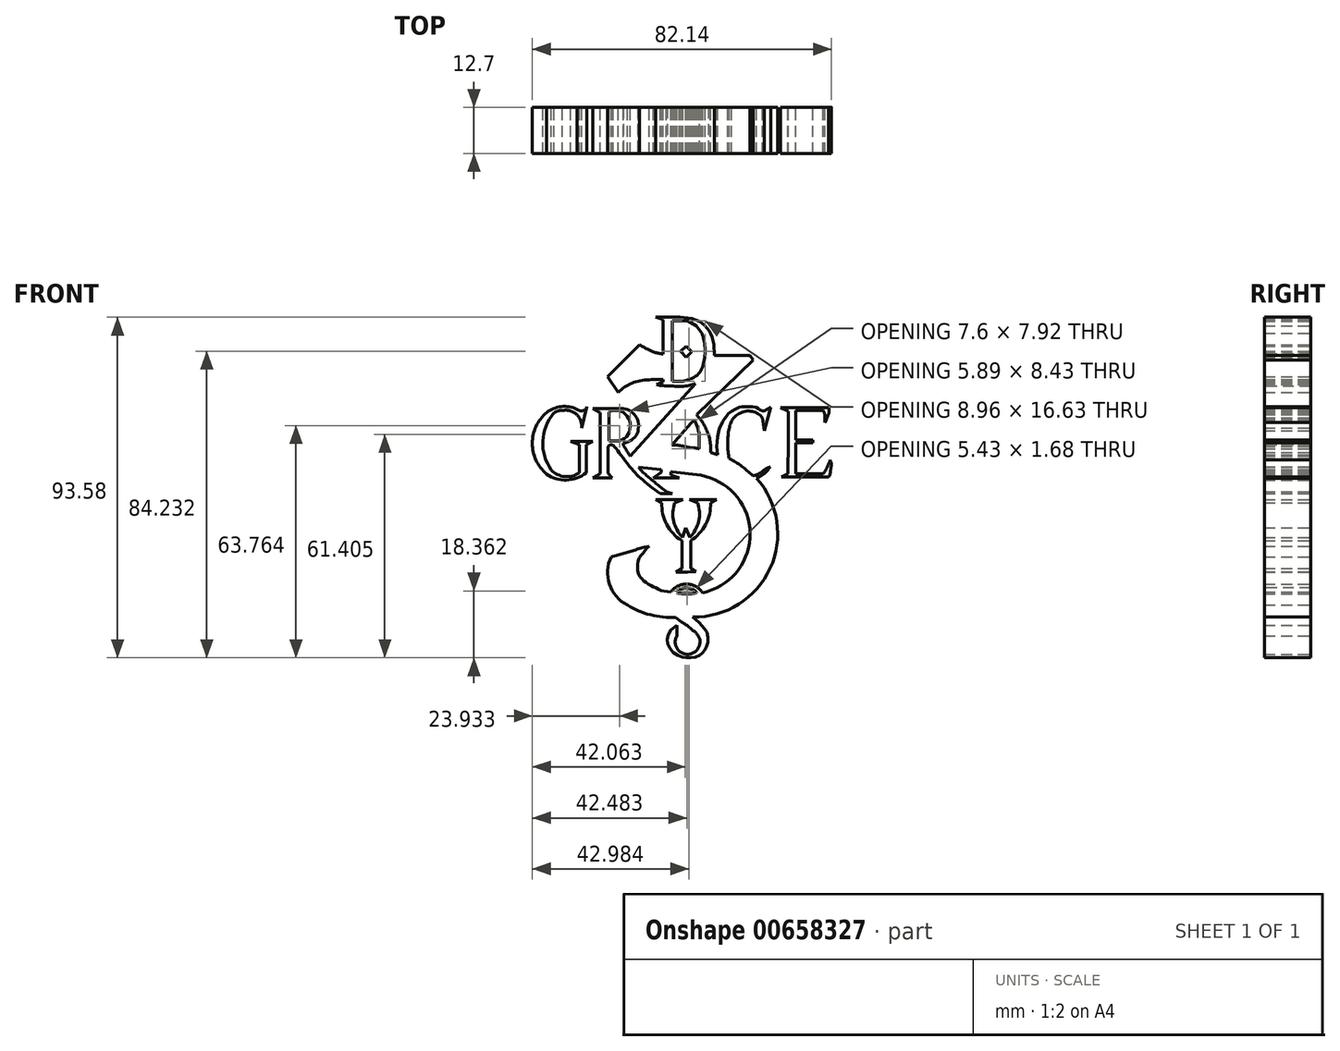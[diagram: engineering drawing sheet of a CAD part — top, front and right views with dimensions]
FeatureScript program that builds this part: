
annotation { "Feature Type Name" : "Feature", "Feature Type Description" : "" }
export const myFeature = defineFeature(function(context is Context, id is Id, definition is map)
    precondition{}
    {
        {
            var Q0;
            Q0=qCreatedBy(makeId("Front.planeOp"),FACE);
            var sketch = newSketch(context, id + "F0", { "sketchPlane" : qUnion([Q0])});
            skLineSegment(sketch, "E0", {"start": v(-8.84, 46.14) * mm, "end": v(-6.93, 45.57) * mm});
            skLineSegment(sketch, "E1", {"start": v(-6.93, 45.57) * mm, "end": v(-6.8, 45.06) * mm});
            skLineSegment(sketch, "E2", {"start": v(-6.8, 45.06) * mm, "end": v(-6.8, 28.36) * mm});
            skLineSegment(sketch, "E3", {"start": v(-6.8, 28.36) * mm, "end": v(-8.53, 27.6) * mm});
            skFitSpline(sketch, "E4", {"points": [v(-8.84, 46.14) * mm, v(-5.12, 46.14) * mm, v(-2.24, 46.14) * mm, v(1.89, 45.57) * mm, v(4.88, 43.67) * mm, v(6.63, 40.9) * mm, v(7.25, 37.23) * mm, v(7.04, 33.67) * mm, v(5.5, 30.27) * mm, v(2.6, 28.1) * mm, v(-1.3, 27.18) * mm, v(-5.02, 27.28) * mm, v(-8.53, 27.6) * mm], "startDerivative": vector(46.15, -0.17) * mm, "endDerivative": vector(-41.2, 9.88) * mm});
            skLineSegment(sketch, "E5", {"start": v(-4.2, 45.12) * mm, "end": v(-4.2, 28.52) * mm});
            skLineSegment(sketch, "E6", {"start": v(-4.2, 45.12) * mm, "end": v(-2.34, 45.12) * mm});
            skLineSegment(sketch, "E7", {"start": v(-2.34, 45.12) * mm, "end": v(0, 45.12) * mm});
            skLineSegment(sketch, "E8", {"start": v(0, 45.12) * mm, "end": v(2.4, 43.78) * mm});
            skLineSegment(sketch, "E9", {"start": v(2.4, 43.78) * mm, "end": v(3.89, 41.77) * mm});
            skFitSpline(sketch, "E10", {"points": [v(3.89, 41.77) * mm, v(4.73, 37.9) * mm, v(4.57, 34.73) * mm, v(3.89, 32.03) * mm, v(2.4, 30.06) * mm, v(0, 28.93) * mm, v(-1.62, 28.52) * mm, v(-4.2, 28.52) * mm], "startDerivative": vector(7.11, -21.44) * mm, "endDerivative": vector(-14.63, 0) * mm});
            skLineSegment(sketch, "E11", {"start": v(-29.8, 3.4) * mm, "end": v(-29.8, 11.14) * mm});
            skLineSegment(sketch, "E12", {"start": v(-29.8, 11.14) * mm, "end": v(-32.14, 12.06) * mm});
            skLineSegment(sketch, "E13", {"start": v(-32.14, 12.06) * mm, "end": v(-26.11, 12.06) * mm});
            skLineSegment(sketch, "E14", {"start": v(-26.11, 12.06) * mm, "end": v(-27.87, 11.14) * mm});
            skLineSegment(sketch, "E15", {"start": v(-27.87, 11.14) * mm, "end": v(-27.87, 3.4) * mm});
            skArc(sketch, "E16", {"start": v(-38.84, 3.06) * mm, "mid": v(-33.3, 1.4) * mm, "end": v(-27.87, 3.4) * mm});
            skArc(sketch, "E17", {"start": v(-38.84, 19.93) * mm, "mid": v(-42.7, 11.5) * mm, "end": v(-38.84, 3.06) * mm});
            skArc(sketch, "E18", {"start": v(-30.38, 20.85) * mm, "mid": v(-34.74, 21.57) * mm, "end": v(-38.84, 19.93) * mm});
            skArc(sketch, "E19", {"start": v(-30.38, 20.85) * mm, "mid": v(-28.86, 20.45) * mm, "end": v(-27.69, 21.5) * mm});
            skLineSegment(sketch, "E20", {"start": v(-29.2, 15.7) * mm, "end": v(-27.69, 21.5) * mm});
            skArc(sketch, "E21", {"start": v(-29.2, 15.7) * mm, "mid": v(-30.56, 19.47) * mm, "end": v(-34.43, 20.5) * mm});
            skArc(sketch, "E22", {"start": v(-36.77, 19.87) * mm, "mid": v(-39.83, 12.13) * mm, "end": v(-37.5, 4.14) * mm});
            skArc(sketch, "E23", {"start": v(-37.5, 4.14) * mm, "mid": v(-33.79, 2.36) * mm, "end": v(-29.8, 3.4) * mm});
            skFitSpline(sketch, "E24", {"points": [v(-36.77, 19.87) * mm, v(-36.16, 20.2) * mm, v(-35.3, 20.5) * mm, v(-34.43, 20.5) * mm], "startDerivative": vector(1.88, 1.04) * mm, "endDerivative": vector(2.53, -0.19) * mm});
            skLineSegment(sketch, "E25", {"start": v(-26.04, 2.02) * mm, "end": v(-20.72, 2.02) * mm});
            skLineSegment(sketch, "E26", {"start": v(-20.72, 2.02) * mm, "end": v(-21.92, 3.27) * mm});
            skLineSegment(sketch, "E27", {"start": v(-21.92, 3.27) * mm, "end": v(-21.92, 10.64) * mm});
            skLineSegment(sketch, "E28", {"start": v(-26.04, 2.02) * mm, "end": v(-24, 3.11) * mm});
            skLineSegment(sketch, "E29", {"start": v(-24, 3.11) * mm, "end": v(-24, 19.85) * mm});
            skLineSegment(sketch, "E30", {"start": v(-24, 19.85) * mm, "end": v(-26.04, 21.1) * mm});
            skLineSegment(sketch, "E31", {"start": v(-26.04, 21.1) * mm, "end": v(-17.68, 21.1) * mm});
            skLineSegment(sketch, "E32", {"start": v(-21.71, 12.13) * mm, "end": v(-21.71, 19.98) * mm});
            skFitSpline(sketch, "E33", {"points": [v(-21.92, 10.64) * mm, v(-21.25, 11.06) * mm, v(-20.45, 10.97) * mm], "startDerivative": vector(1.29, 1.1) * mm, "endDerivative": vector(1.65, -0.43) * mm});
            skFitSpline(sketch, "E34", {"points": [v(-21.71, 19.98) * mm, v(-21.08, 20.42) * mm, v(-18.79, 20.42) * mm, v(-17.14, 19.52) * mm, v(-16.05, 17.88) * mm, v(-15.85, 15.84) * mm, v(-16.5, 13.75) * mm, v(-18.04, 12.4) * mm, v(-19.88, 12.12) * mm, v(-21.71, 12.13) * mm], "startDerivative": vector(6.77, 6.93) * mm, "endDerivative": vector(-16.76, -0.86) * mm});
            skFitSpline(sketch, "E35", {"points": [v(-17.68, 21.1) * mm, v(-16.38, 20.72) * mm, v(-15.2, 19.9) * mm, v(-14.1, 18.7) * mm, v(-13.66, 17.56) * mm, v(-13.57, 15.49) * mm, v(-13.98, 14) * mm, v(-14.96, 12.82) * mm, v(-16.14, 12.02) * mm, v(-17.68, 11.55) * mm], "startDerivative": vector(12.97, -2.59) * mm, "endDerivative": vector(-13.49, -2.9) * mm});
            skFitSpline(sketch, "E36", {"points": [v(-20.45, 10.97) * mm, v(-19.41, 9.65) * mm, v(-17.78, 7.47) * mm, v(-15.56, 4.58) * mm, v(-14.01, 2.9) * mm, v(-12.42, 1.49) * mm, v(-10.04, -0.48) * mm, v(-7.57, -2.28) * mm], "startDerivative": vector(8.68, -10.98) * mm, "endDerivative": vector(15.96, -11.26) * mm});
            skFitSpline(sketch, "E37", {"points": [v(-17.68, 11.55) * mm, v(-17.68, 10.97) * mm, v(-17.07, 9.94) * mm, v(-15.85, 7.96) * mm, v(-15.02, 6.63) * mm, v(-13.89, 5.34) * mm, v(-12.38, 3.62) * mm, v(-10.83, 2.24) * mm, v(-9.45, 1.07) * mm, v(-7.74, -0.36) * mm, v(-5.9, -1.78) * mm], "startDerivative": vector(-1.42, -9.84) * mm, "endDerivative": vector(16.07, -12.2) * mm});
            skLineSegment(sketch, "E38", {"start": v(-7.57, -2.28) * mm, "end": v(-4.26, -2.28) * mm});
            skLineSegment(sketch, "E39", {"start": v(-5.9, -1.78) * mm, "end": v(-4.26, -2.28) * mm});
            skLineSegment(sketch, "E40", {"start": v(-4.59, 6.65) * mm, "end": v(-4.59, 2.75) * mm});
            skLineSegment(sketch, "E41", {"start": v(-4.59, 2.75) * mm, "end": v(-2.4, 2) * mm});
            skLineSegment(sketch, "E42", {"start": v(-2.4, 2) * mm, "end": v(-9.44, 2) * mm});
            skLineSegment(sketch, "E43", {"start": v(-9.44, 2) * mm, "end": v(-7.26, 3.49) * mm});
            skLineSegment(sketch, "E44", {"start": v(-7.26, 3.49) * mm, "end": v(-7.26, 6.65) * mm});
            skLineSegment(sketch, "E45", {"start": v(-4.59, 6.65) * mm, "end": v(-0.47, 6.65) * mm});
            skLineSegment(sketch, "E46", {"start": v(-4.43, 8.82) * mm, "end": v(-0.47, 8.82) * mm});
            skFitSpline(sketch, "E47", {"points": [v(-4.43, 8.82) * mm, v(-4.43, 11.51) * mm, v(-4.24, 13.86) * mm, v(-3.45, 16.33) * mm, v(-2.48, 18.34) * mm, v(-1.31, 19.97) * mm, v(-0.47, 20.64) * mm], "startDerivative": vector(-0.41, 14.69) * mm, "endDerivative": vector(6.95, 4.72) * mm});
            skFitSpline(sketch, "E48", {"points": [v(-7.26, 6.65) * mm, v(-7.26, 10.37) * mm, v(-6.9, 12.9) * mm, v(-6.06, 15.25) * mm, v(-4.43, 18.07) * mm, v(-2.13, 20.67) * mm, v(-1.24, 21.47) * mm, v(-0.47, 22.02) * mm], "startDerivative": vector(-0.45, 21.88) * mm, "endDerivative": vector(8.8, 5.98) * mm});
            skLineSegment(sketch, "E49.MirrorCS", {"start": v(1.46, 2) * mm, "end": v(8.5, 2) * mm});
            skLineSegment(sketch, "E50.MirrorCS", {"start": v(3.64, 2.75) * mm, "end": v(1.46, 2) * mm});
            skLineSegment(sketch, "E51.MirrorCS", {"start": v(8.5, 2) * mm, "end": v(6.32, 3.49) * mm});
            skFitSpline(sketch, "E52.MirrorCS", {"points": [v(6.32, 6.65) * mm, v(6.32, 10.37) * mm, v(5.96, 12.9) * mm, v(5.12, 15.25) * mm, v(3.48, 18.07) * mm, v(1.18, 20.67) * mm, v(0.29, 21.47) * mm, v(-0.47, 22.02) * mm], "startDerivative": vector(0.45, 21.88) * mm, "endDerivative": vector(-8.8, 5.98) * mm});
            skLineSegment(sketch, "E53.MirrorCS", {"start": v(3.64, 6.65) * mm, "end": v(3.64, 2.75) * mm});
            skLineSegment(sketch, "E54.MirrorCS", {"start": v(3.17, 8.74) * mm, "end": v(-0.47, 8.82) * mm});
            skFitSpline(sketch, "E55.MirrorCS", {"points": [v(3.17, 8.74) * mm, v(3.13, 11.7) * mm, v(3.1, 13.92) * mm, v(2.5, 16.33) * mm, v(1.53, 18.34) * mm, v(0.36, 19.97) * mm, v(-0.47, 20.64) * mm], "startDerivative": vector(0.41, 14.69) * mm, "endDerivative": vector(-6.95, 4.72) * mm});
            skLineSegment(sketch, "E56.MirrorCS", {"start": v(3.64, 6.65) * mm, "end": v(-0.47, 6.65) * mm});
            skLineSegment(sketch, "E57.MirrorCS", {"start": v(6.32, 3.49) * mm, "end": v(6.32, 6.65) * mm});
            skLineSegment(sketch, "E58", {"start": v(20.96, 15) * mm, "end": v(22.74, 21.4) * mm});
            skLineSegment(sketch, "E59", {"start": v(22.74, 21.4) * mm, "end": v(21.02, 20.4) * mm});
            skLineSegment(sketch, "E60", {"start": v(20.96, 15) * mm, "end": v(20.55, 18.52) * mm});
            skFitSpline(sketch, "E61", {"points": [v(21.02, 20.4) * mm, v(20.29, 20.4) * mm, v(19.36, 21.05) * mm, v(18.28, 21.47) * mm, v(15.64, 21.55) * mm, v(14.47, 21.47) * mm, v(11.75, 20.09) * mm, v(10.33, 18.62) * mm, v(9.38, 17.03) * mm, v(8.43, 14.74) * mm, v(7.99, 10.65) * mm, v(8.38, 7.67) * mm, v(10.37, 3.78) * mm, v(13.31, 1.84) * mm, v(17.54, 1.45) * mm, v(20.03, 2.54) * mm, v(21.72, 3.84) * mm, v(22.62, 5.08) * mm], "startDerivative": vector(-22.13, -4.12) * mm, "endDerivative": vector(16.3, 26.76) * mm});
            skFitSpline(sketch, "E62", {"points": [v(22.62, 5.08) * mm, v(21.02, 4.14) * mm, v(19.53, 3.14) * mm, v(17.84, 2.6) * mm, v(15.9, 2.7) * mm, v(14.26, 3.19) * mm, v(12.47, 5.08) * mm, v(11.42, 7.32) * mm, v(10.97, 10.26) * mm, v(10.97, 12.4) * mm, v(11.27, 15.14) * mm, v(12.02, 17.63) * mm], "startDerivative": vector(-19.62, -10.9) * mm, "endDerivative": vector(10.62, 19.74) * mm});
            skFitSpline(sketch, "E63", {"points": [v(12.02, 17.63) * mm, v(13.36, 19.17) * mm, v(16.05, 20.32) * mm, v(18.74, 19.92) * mm, v(20.55, 18.52) * mm], "startDerivative": vector(3.75, 7.8) * mm, "endDerivative": vector(6.9, -6.59) * mm});
            skLineSegment(sketch, "E64", {"start": v(25.77, 2.19) * mm, "end": v(38.73, 2.19) * mm});
            skLineSegment(sketch, "E65", {"start": v(29.69, 3.1) * mm, "end": v(37.11, 3.1) * mm});
            skFitSpline(sketch, "E66", {"points": [v(37.11, 3.1) * mm, v(38.14, 4.65) * mm, v(38.55, 5.54) * mm, v(39.1, 6.94) * mm], "startDerivative": vector(2.84, 2.62) * mm, "endDerivative": vector(0, 4.56) * mm});
            skFitSpline(sketch, "E67", {"points": [v(38.73, 2.19) * mm, v(39.27, 4.34) * mm, v(39.44, 5.75) * mm, v(39.1, 6.94) * mm], "startDerivative": vector(3.1, 4.74) * mm, "endDerivative": vector(-2.89, 4.9) * mm});
            skLineSegment(sketch, "E68", {"start": v(29.69, 3.1) * mm, "end": v(29.69, 11.62) * mm});
            skLineSegment(sketch, "E69", {"start": v(29.69, 11.62) * mm, "end": v(34.33, 11.62) * mm});
            skFitSpline(sketch, "E70.MirrorCS", {"points": [v(37.11, 20.48) * mm, v(37.6, 19.53) * mm, v(37.64, 18.76) * mm, v(37.67, 17.2) * mm], "startDerivative": vector(2.84, -2.62) * mm, "endDerivative": vector(0, -4.56) * mm});
            skLineSegment(sketch, "E71.MirrorCS", {"start": v(25.46, 21.25) * mm, "end": v(27.68, 20.23) * mm});
            skLineSegment(sketch, "E72.MirrorCS", {"start": v(29.69, 12.42) * mm, "end": v(34.39, 12.44) * mm});
            skLineSegment(sketch, "E73.MirrorCS", {"start": v(25.46, 21.25) * mm, "end": v(38.73, 21.25) * mm});
            skLineSegment(sketch, "E74.MirrorCS", {"start": v(29.65, 20.48) * mm, "end": v(37.11, 20.48) * mm});
            skLineSegment(sketch, "E75.MirrorCS", {"start": v(29.65, 20.48) * mm, "end": v(29.69, 12.42) * mm});
            skFitSpline(sketch, "E76.MirrorCS", {"points": [v(38.73, 21.25) * mm, v(38.76, 19.92) * mm, v(38.38, 18.76) * mm, v(37.67, 17.2) * mm], "startDerivative": vector(1.5, -3.48) * mm, "endDerivative": vector(-2.89, -4.9) * mm});
            skLineSegment(sketch, "E77", {"start": v(27.68, 20.23) * mm, "end": v(27.68, 12.18) * mm});
            skLineSegment(sketch, "E78", {"start": v(34.39, 12.44) * mm, "end": v(34.33, 11.62) * mm});
            skLineSegment(sketch, "E79", {"start": v(25.77, 2.19) * mm, "end": v(27.51, 3.1) * mm});
            skLineSegment(sketch, "E80", {"start": v(27.51, 3.1) * mm, "end": v(27.68, 12.18) * mm});
            skLineSegment(sketch, "E81", {"start": v(-8.78, -3.94) * mm, "end": v(-1.33, -3.94) * mm});
            skLineSegment(sketch, "E82", {"start": v(-1.33, -3.94) * mm, "end": v(-3.56, -4.8) * mm});
            skLineSegment(sketch, "E83", {"start": v(-8.78, -3.94) * mm, "end": v(-7.13, -4.89) * mm});
            skArc(sketch, "E84", {"start": v(-7.13, -4.89) * mm, "mid": v(-5.8, -10.81) * mm, "end": v(-1.64, -15.23) * mm});
            skArc(sketch, "E85", {"start": v(-3.56, -4.8) * mm, "mid": v(-3.9, -9.9) * mm, "end": v(-1.42, -14.37) * mm});
            skLineSegment(sketch, "E86", {"start": v(-1.42, -14.37) * mm, "end": v(-0.57, -11.74) * mm});
            skLineSegment(sketch, "E87", {"start": v(-1.64, -15.23) * mm, "end": v(-1.64, -22.9) * mm});
            skLineSegment(sketch, "E88", {"start": v(-1.64, -22.9) * mm, "end": v(-3.22, -23.9) * mm});
            skLineSegment(sketch, "E89", {"start": v(-3.22, -23.9) * mm, "end": v(0, -23.9) * mm});
            skLineSegment(sketch, "E90.MirrorCS", {"start": v(7.9, -3.94) * mm, "end": v(0.46, -3.94) * mm});
            skLineSegment(sketch, "E91.MirrorCS", {"start": v(0.77, -22.9) * mm, "end": v(2.23, -23.83) * mm});
            skLineSegment(sketch, "E92.MirrorCS", {"start": v(0.46, -3.94) * mm, "end": v(2.68, -4.8) * mm});
            skLineSegment(sketch, "E93.MirrorCS", {"start": v(0.77, -15.23) * mm, "end": v(0.77, -22.9) * mm});
            skLineSegment(sketch, "E94.MirrorCS", {"start": v(7.9, -3.94) * mm, "end": v(6.26, -4.89) * mm});
            skArc(sketch, "E95.MirrorCS", {"start": v(6.26, -4.89) * mm, "mid": v(4.93, -10.81) * mm, "end": v(0.77, -15.23) * mm});
            skArc(sketch, "E96.MirrorCS", {"start": v(2.68, -4.8) * mm, "mid": v(3.03, -9.9) * mm, "end": v(0.54, -14.37) * mm});
            skPoint(sketch, "E97.orphan", {"position": v(-0.57, -3.29) * mm});
            skLineSegment(sketch, "E98", {"start": v(0, -23.9) * mm, "end": v(2.23, -23.83) * mm});
            skLineSegment(sketch, "E99", {"start": v(0.54, -14.37) * mm, "end": v(-0.57, -11.74) * mm});
            skLineSegment(sketch, "E100", {"start": v(1.96, -34) * mm, "end": v(5.05, -32.55) * mm});
            skLineSegment(sketch, "E101", {"start": v(-3, -38.46) * mm, "end": v(-3, -41.38) * mm});
            skArc(sketch, "E102", {"start": v(-3, -41.38) * mm, "mid": v(-0.05, -46.5) * mm, "end": v(2.9, -41.38) * mm});
            skArc(sketch, "E103", {"start": v(5.05, -32.55) * mm, "mid": v(-0.35, -27.21) * mm, "end": v(-5.75, -32.55) * mm});
            skFitSpline(sketch, "E104", {"points": [v(1.96, -34) * mm, v(2.57, -32.5) * mm, v(2.78, -31.32) * mm, v(2.57, -29.8) * mm, v(1.96, -28.98) * mm, v(0.69, -28.42) * mm, v(-1.25, -28.32) * mm, v(-2.93, -29.64) * mm, v(-3.13, -31.27) * mm, v(-2.78, -33.05) * mm, v(-1.8, -34) * mm, v(0, -35.4) * mm, v(1.4, -36.25) * mm, v(2.83, -37.49) * mm, v(4.1, -38.86) * mm, v(5.17, -40.34) * mm, v(5.58, -42.9) * mm, v(4.87, -44.88) * mm, v(4, -46.2) * mm, v(2.73, -47.07) * mm, v(0.43, -47.43) * mm, v(-1.35, -47.27) * mm, v(-3.8, -46.1) * mm, v(-5.43, -43.8) * mm, v(-5.58, -41.82) * mm, v(-3, -38.46) * mm], "startDerivative": vector(18.87, 42.96) * mm, "endDerivative": vector(88.6, 43.3) * mm});
            skFitSpline(sketch, "E105", {"points": [v(-5.75, -32.55) * mm, v(-5.33, -34.33) * mm, v(-3.9, -35.9) * mm, v(-2.01, -37.39) * mm, v(-0.43, -38.4) * mm, v(1.15, -39.68) * mm, v(2.42, -40.8) * mm, v(2.9, -41.38) * mm], "startDerivative": vector(1.49, -12.8) * mm, "endDerivative": vector(4.44, -5.84) * mm});
            skLineSegment(sketch, "E106", {"start": v(-1.91, 36.73) * mm, "end": v(-0.45, 38.23) * mm});
            skLineSegment(sketch, "E107", {"start": v(-0.45, 38.23) * mm, "end": v(1.12, 36.7) * mm});
            skLineSegment(sketch, "E108", {"start": v(-1.91, 36.73) * mm, "end": v(-0.49, 35.2) * mm});
            skLineSegment(sketch, "E109", {"start": v(-0.49, 35.2) * mm, "end": v(1.12, 36.7) * mm});
            skLineSegment(sketch, "E110", {"start": v(-22, 29.76) * mm, "end": v(-13.28, 38.62) * mm});
            skLineSegment(sketch, "E111", {"start": v(-22, 29.76) * mm, "end": v(-19.12, 25.5) * mm});
            skFitSpline(sketch, "E112", {"points": [v(-13.28, 38.62) * mm, v(-11.58, 37.66) * mm, v(-10.34, 37.06) * mm, v(-9, 36.46) * mm, v(-7.6, 36.16) * mm, v(-6.8, 36.07) * mm], "startDerivative": vector(7.66, -4.29) * mm, "endDerivative": vector(6, 0.06) * mm});
            skLineSegment(sketch, "E113", {"start": v(-4.2, 35.68) * mm, "end": v(-0.93, 35.68) * mm});
            skLineSegment(sketch, "E114", {"start": v(0.02, 35.68) * mm, "end": v(4.7, 35.68) * mm});
            skLineSegment(sketch, "E115", {"start": v(7.28, 35.68) * mm, "end": v(17.1, 35.68) * mm});
            skLineSegment(sketch, "E116", {"start": v(17.1, 35.68) * mm, "end": v(17.97, 34.4) * mm});
            skLineSegment(sketch, "E117", {"start": v(17.97, 34.4) * mm, "end": v(2.42, 19.38) * mm});
            skLineSegment(sketch, "E118", {"start": v(-15.85, 7.96) * mm, "end": v(2.15, 27.92) * mm});
            skLineSegment(sketch, "E119", {"start": v(1.76, 17.94) * mm, "end": v(-4.44, 10.97) * mm});
            skFitSpline(sketch, "E120", {"points": [v(-4.44, 10.97) * mm, v(-2.83, 10.97) * mm, v(-0.92, 10.64) * mm, v(0.98, 10.26) * mm, v(2.76, 10.13) * mm, v(3.16, 10.01) * mm], "startDerivative": vector(7.74, 0.33) * mm, "endDerivative": vector(4.72, -0.31) * mm});
            skLineSegment(sketch, "E121", {"start": v(6.35, 8.95) * mm, "end": v(8.2, 8.33) * mm});
            skArc(sketch, "E122", {"start": v(17.84, 2.6) * mm, "mid": v(14.81, 5.2) * mm, "end": v(11.42, 7.32) * mm});
            skArc(sketch, "E123", {"start": v(1.4, -36.25) * mm, "mid": v(22.6, -22.9) * mm, "end": v(18.92, 1.9) * mm});
            skArc(sketch, "E124", {"start": v(4.13, -29.6) * mm, "mid": v(17.08, -14.55) * mm, "end": v(6.12, 2) * mm});
            skArc(sketch, "E125", {"start": v(-2.93, -29.64) * mm, "mid": v(-0.18, -29.9) * mm, "end": v(2.57, -29.6) * mm});
            skArc(sketch, "E126", {"start": v(-21.06, -19.67) * mm, "mid": v(-21.52, -27.21) * mm, "end": v(-16.63, -32.97) * mm});
            skFitSpline(sketch, "E127", {"points": [v(-10.66, -16.74) * mm, v(-12.08, -18.38) * mm, v(-13.46, -20.32) * mm, v(-13.81, -22.56) * mm, v(-13.3, -24.86) * mm, v(-12.08, -26.28) * mm, v(-10.6, -27.35) * mm, v(-8.82, -28.22) * mm, v(-7.09, -29.03) * mm, v(-4.65, -29.35) * mm], "startDerivative": vector(-15.25, -13.01) * mm, "endDerivative": vector(21.73, -1.19) * mm});
            skFitSpline(sketch, "E128", {"points": [v(-21.06, -19.67) * mm, v(-10.66, -16.74) * mm], "startDerivative": vector(10.7, 2.85) * mm, "endDerivative": vector(10.7, 2.85) * mm});
            skArc(sketch, "E129", {"start": v(-16.63, -32.97) * mm, "mid": v(-10.22, -35.65) * mm, "end": v(-3.31, -36.4) * mm});
            skLineSegment(sketch, "E130", {"start": v(3.64, 2.75) * mm, "end": v(-4.23, 3.61) * mm});
            skLineSegment(sketch, "E131", {"start": v(-7.26, 4.22) * mm, "end": v(-13.56, 4.95) * mm});
            skFitSpline(sketch, "E132", {"points": [v(-19.12, 25.5) * mm, v(-17.37, 26.92) * mm, v(-15.53, 27.94) * mm, v(-13.34, 28.65) * mm, v(-10.64, 28.96) * mm, v(-7.99, 29.06) * mm, v(-6.8, 29.04) * mm], "startDerivative": vector(10.24, 8.86) * mm, "endDerivative": vector(9.25, 1.35) * mm});
            skLineSegment(sketch, "E133", {"start": v(-4.23, 3.61) * mm, "end": v(-4.59, 3.61) * mm});
            skLineSegment(sketch, "E134", {"start": v(-3.31, -36.4) * mm, "end": v(1.4, -36.25) * mm});
            skLineSegment(sketch, "E135", {"start": v(-4.65, -29.35) * mm, "end": v(-2.93, -29.64) * mm});
            skLineSegment(sketch, "E136", {"start": v(-7.26, 4.22) * mm, "end": v(-4.59, 3.61) * mm});
            skLineSegment(sketch, "E137", {"start": v(3.64, 2.75) * mm, "end": v(6.12, 2) * mm});
            skLineSegment(sketch, "E138", {"start": v(-4.44, 10.97) * mm, "end": v(-7.18, 11.42) * mm});
            skLineSegment(sketch, "E139", {"start": v(3.16, 10.01) * mm, "end": v(6.35, 8.95) * mm});
            skLineSegment(sketch, "E140", {"start": v(8.2, 8.33) * mm, "end": v(11.42, 7.32) * mm});
            skLineSegment(sketch, "E141", {"start": v(17.84, 2.6) * mm, "end": v(18.92, 1.9) * mm});
            skSolve(sketch);
        }
        {
            var Q0;
            Q0=makeQuery(id+"F0.imprint","IMPRINT",FACE,{"disambiguationData":[TD([[makeQuery(id+"F0.imprint","IMPRINT",EDGE,{"derivedFrom":sQuery(id+"F0.wireOp",EDGE,"E11")}),-1.0]])]});
            var Q1;
            Q1=makeQuery(id+"F0.imprint","IMPRINT",FACE,{"disambiguationData":[TD([[makeQuery(id+"F0.imprint","IMPRINT",EDGE,{"derivedFrom":sQuery(id+"F0.wireOp",EDGE,"E64")}),1.0]])]});
            var Q2;
            Q2=makeQuery(id+"F0.imprint","IMPRINT",FACE,{"disambiguationData":[TD([[makeQuery(id+"F0.imprint","IMPRINT",EDGE,{"derivedFrom":sQuery(id+"F0.wireOp",EDGE,"E81")}),-1.0]])]});
            var Q3;
            Q3=makeQuery(id+"F0.imprint","IMPRINT",FACE,{"disambiguationData":[TD([[makeQuery(id+"F0.imprint","IMPRINT",EDGE,{"derivedFrom":sQuery(id+"F0.wireOp",EDGE,"E110")}),-1.0]])]});
            var Q4;
            {var subQ3=sQuery(id+"F0.wireOp",EDGE,"E119");Q4=makeQuery(id+"F0.imprint","IMPRINT",FACE,{"disambiguationData":[TD([[makeQuery(id+"F0.imprint","IMPRINT",EDGE,{"derivedFrom":subQ3}),-1.0]])]});}
            var Q5;
            {var subQ0=sQuery(id+"F0.wireOp",EDGE,"E122");Q5=makeQuery(id+"F0.imprint","IMPRINT",FACE,{"disambiguationData":[TD([[makeQuery(id+"F0.imprint","IMPRINT",EDGE,{"derivedFrom":subQ0}),1.0]])]});}
            var Q6;
            Q6=makeQuery(id+"F0.imprint","IMPRINT",FACE,{"disambiguationData":[TD([[makeQuery(id+"F0.imprint","IMPRINT",EDGE,{"derivedFrom":sQuery(id+"F0.wireOp",EDGE,"E126")}),1.0]])]});
            var Q7;
            {var subQ0=sQuery(id+"F0.wireOp",EDGE,"E48");Q7=makeQuery(id+"F0.imprint","IMPRINT",FACE,{"disambiguationData":[TD([[makeQuery(id+"F0.imprint","IMPRINT",EDGE,{"derivedFrom":subQ0}),1.0]])]});}
            var Q8;
            Q8=makeQuery(id+"F0.imprint","IMPRINT",FACE,{"disambiguationData":[TD([[makeQuery(id+"F0.imprint","IMPRINT",EDGE,{"derivedFrom":sQuery(id+"F0.wireOp",EDGE,"E25")}),1.0]])]});
            var Q9;
            Q9=makeQuery(id+"F0.imprint","IMPRINT",FACE,{"disambiguationData":[TD([[makeQuery(id+"F0.imprint","IMPRINT",EDGE,{"derivedFrom":sQuery(id+"F0.wireOp",EDGE,"E58")}),1.0]])]});
            var Q10;
            {var subQ8=sQuery(id+"F0.wireOp",EDGE,"E51.MirrorCS");Q10=makeQuery(id+"F0.imprint","IMPRINT",FACE,{"disambiguationData":[TD([[makeQuery(id+"F0.imprint","IMPRINT",EDGE,{"derivedFrom":subQ8}),-1.0]])]});}
            var Q11;
            {var subQ7=sQuery(id+"F0.wireOp",EDGE,"E0");Q11=makeQuery(id+"F0.imprint","IMPRINT",FACE,{"disambiguationData":[TD([[makeQuery(id+"F0.imprint","IMPRINT",EDGE,{"derivedFrom":subQ7}),1.0]])]});}
            var Q12;
            {var subQ4=sQuery(id+"F0.wireOp",EDGE,"E46");Q12=makeQuery(id+"F0.imprint","IMPRINT",FACE,{"disambiguationData":[TD([[makeQuery(id+"F0.imprint","IMPRINT",EDGE,{"derivedFrom":subQ4}),1.0]])]});}
            var Q13;
            {var subQ4=sQuery(id+"F0.wireOp",EDGE,"E106");Q13=makeQuery(id+"F0.imprint","IMPRINT",FACE,{"disambiguationData":[TD([[makeQuery(id+"F0.imprint","IMPRINT",EDGE,{"derivedFrom":subQ4}),-1.0]])]});}
            var Q14;
            {var subQ19=sQuery(id+"F0.wireOp",EDGE,"E41");Q14=makeQuery(id+"F0.imprint","IMPRINT",FACE,{"disambiguationData":[TD([[makeQuery(id+"F0.imprint","IMPRINT",EDGE,{"derivedFrom":subQ19}),-1.0]])]});}
            var Q15;
            {var subQ6=sQuery(id+"F0.wireOp",EDGE,"E100");Q15=makeQuery(id+"F0.imprint","IMPRINT",FACE,{"disambiguationData":[TD([[makeQuery(id+"F0.imprint","IMPRINT",EDGE,{"derivedFrom":subQ6}),1.0]])]});}
            var Q16;
            {var subQ14=sQuery(id+"F0.wireOp",EDGE,"E46");Q16=makeQuery(id+"F0.imprint","IMPRINT",FACE,{"disambiguationData":[TD([[makeQuery(id+"F0.imprint","IMPRINT",EDGE,{"derivedFrom":subQ14}),-1.0]])]});}
            var Q17;
            {var subQ0=sQuery(id+"F0.wireOp",EDGE,"E140");Q17=makeQuery(id+"F0.imprint","IMPRINT",FACE,{"disambiguationData":[TD([[makeQuery(id+"F0.imprint","IMPRINT",EDGE,{"derivedFrom":subQ0}),-1.0]])]});}
            var Q18;
            {var subQ3=sQuery(id+"F0.wireOp",EDGE,"E141");Q18=makeQuery(id+"F0.imprint","IMPRINT",FACE,{"disambiguationData":[TD([[makeQuery(id+"F0.imprint","IMPRINT",EDGE,{"derivedFrom":subQ3}),1.0]])]});}
            var Q19;
            {var subQ0=sQuery(id+"F0.wireOp",EDGE,"E134");Q19=makeQuery(id+"F0.imprint","IMPRINT",FACE,{"disambiguationData":[TD([[makeQuery(id+"F0.imprint","IMPRINT",EDGE,{"derivedFrom":subQ0}),1.0]])]});}
            var Q20;
            {var subQ1=sQuery(id+"F0.wireOp",EDGE,"E101");Q20=makeQuery(id+"F0.imprint","IMPRINT",FACE,{"disambiguationData":[TD([[makeQuery(id+"F0.imprint","IMPRINT",EDGE,{"derivedFrom":subQ1}),-1.0]])]});}
            var Q21;
            {var subQ5=sQuery(id+"F0.wireOp",EDGE,"E138");Q21=makeQuery(id+"F0.imprint","IMPRINT",FACE,{"disambiguationData":[TD([[makeQuery(id+"F0.imprint","IMPRINT",EDGE,{"derivedFrom":subQ5}),-1.0]])]});}
            extrude(context, id + "F1", {"entities" : qUnion([Q0, Q1, Q2, Q3, Q4, Q5, Q6, Q7, Q8, Q9, Q10, Q11, Q12, Q13, Q14, Q15, Q16, Q17, Q18, Q19, Q20, Q21]), "depth" : 12.7 * mm, "offsetDistance" : 25.4 * mm});
        }
    });
